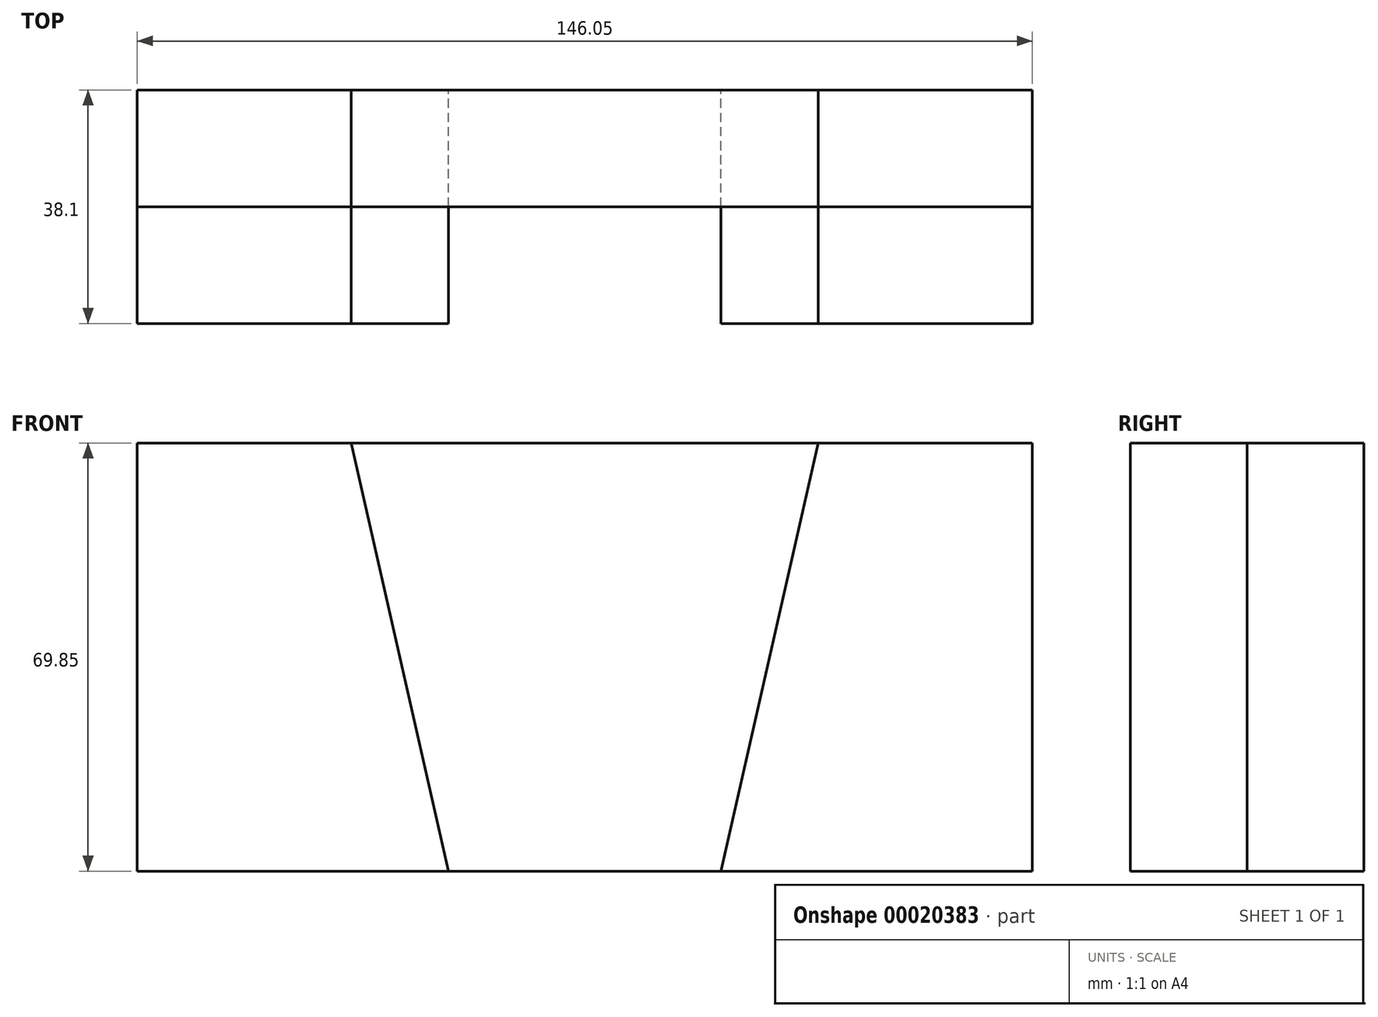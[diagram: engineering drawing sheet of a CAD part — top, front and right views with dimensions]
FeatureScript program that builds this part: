
annotation { "Feature Type Name" : "Feature", "Feature Type Description" : "" }
export const myFeature = defineFeature(function(context is Context, id is Id, definition is map)
    precondition{}
    {
        {
            var Q0;
            Q0=qCreatedBy(makeId("Front.planeOp"),FACE);
            var sketch = newSketch(context, id + "F0", { "sketchPlane" : qUnion([Q0])});
            skLineSegment(sketch, "E0.bottom", {"start": v(-74.9, 43.41) * mm, "end": v(71.16, 43.41) * mm});
            skLineSegment(sketch, "E0.top", {"start": v(-74.9, -26.44) * mm, "end": v(71.16, -26.44) * mm});
            skLineSegment(sketch, "E0.left", {"start": v(-74.9, 43.41) * mm, "end": v(-74.9, -26.44) * mm});
            skLineSegment(sketch, "E0.right", {"start": v(71.16, 43.41) * mm, "end": v(71.16, -26.44) * mm});
            skLineSegment(sketch, "E1", {"start": v(71.16, -26.44) * mm, "end": v(20.36, -26.44) * mm});
            skLineSegment(sketch, "E2", {"start": v(20.36, -26.44) * mm, "end": v(-24.1, -26.44) * mm});
            skLineSegment(sketch, "E3", {"start": v(71.16, 43.41) * mm, "end": v(36.23, 43.41) * mm});
            skLineSegment(sketch, "E4", {"start": v(36.23, 43.41) * mm, "end": v(-31.59, 43.41) * mm});
            skLineSegment(sketch, "E5", {"start": v(20.36, -26.44) * mm, "end": v(36.23, 43.41) * mm});
            skLineSegment(sketch, "E6.MirrorCS", {"start": v(-24.1, -26.44) * mm, "end": v(-39.97, 43.41) * mm});
            skLineSegment(sketch, "E7.MirrorCS", {"start": v(-74.9, 43.41) * mm, "end": v(-39.97, 43.41) * mm});
            skLineSegment(sketch, "E8.MirrorCS", {"start": v(-74.9, -26.44) * mm, "end": v(-24.1, -26.44) * mm});
            skPoint(sketch, "E9.end.orphan", {"position": v(-1.87, 43.41) * mm});
            skPoint(sketch, "E9.start.orphan", {"position": v(-1.87, -26.44) * mm});
            skSolve(sketch);
        }
        {
            var Q0;
            Q0=makeQuery(id+"F0.imprint","IMPRINT",FACE,{"disambiguationData":[TD([[makeQuery(id+"F0.imprint","IMPRINT",EDGE,{"derivedFrom":sQuery(id+"F0.wireOp",EDGE,"E0.left")}),1.0]])]});
            var Q1;
            Q1=makeQuery(id+"F0.imprint","IMPRINT",FACE,{"disambiguationData":[TD([[makeQuery(id+"F0.imprint","IMPRINT",EDGE,{"derivedFrom":sQuery(id+"F0.wireOp",EDGE,"E0.right")}),-1.0]])]});
            extrude(context, id + "F1", {"entities" : qUnion([Q0, Q1]), "depth" : 38.1 * mm});
        }
        {
            var Q0;
            Q0 = qSketchRegion(id + "F0", true);
            extrude(context, id + "F2", {"entities" : qUnion([Q0]), "depth" : 19.05 * mm});
        }
    });
